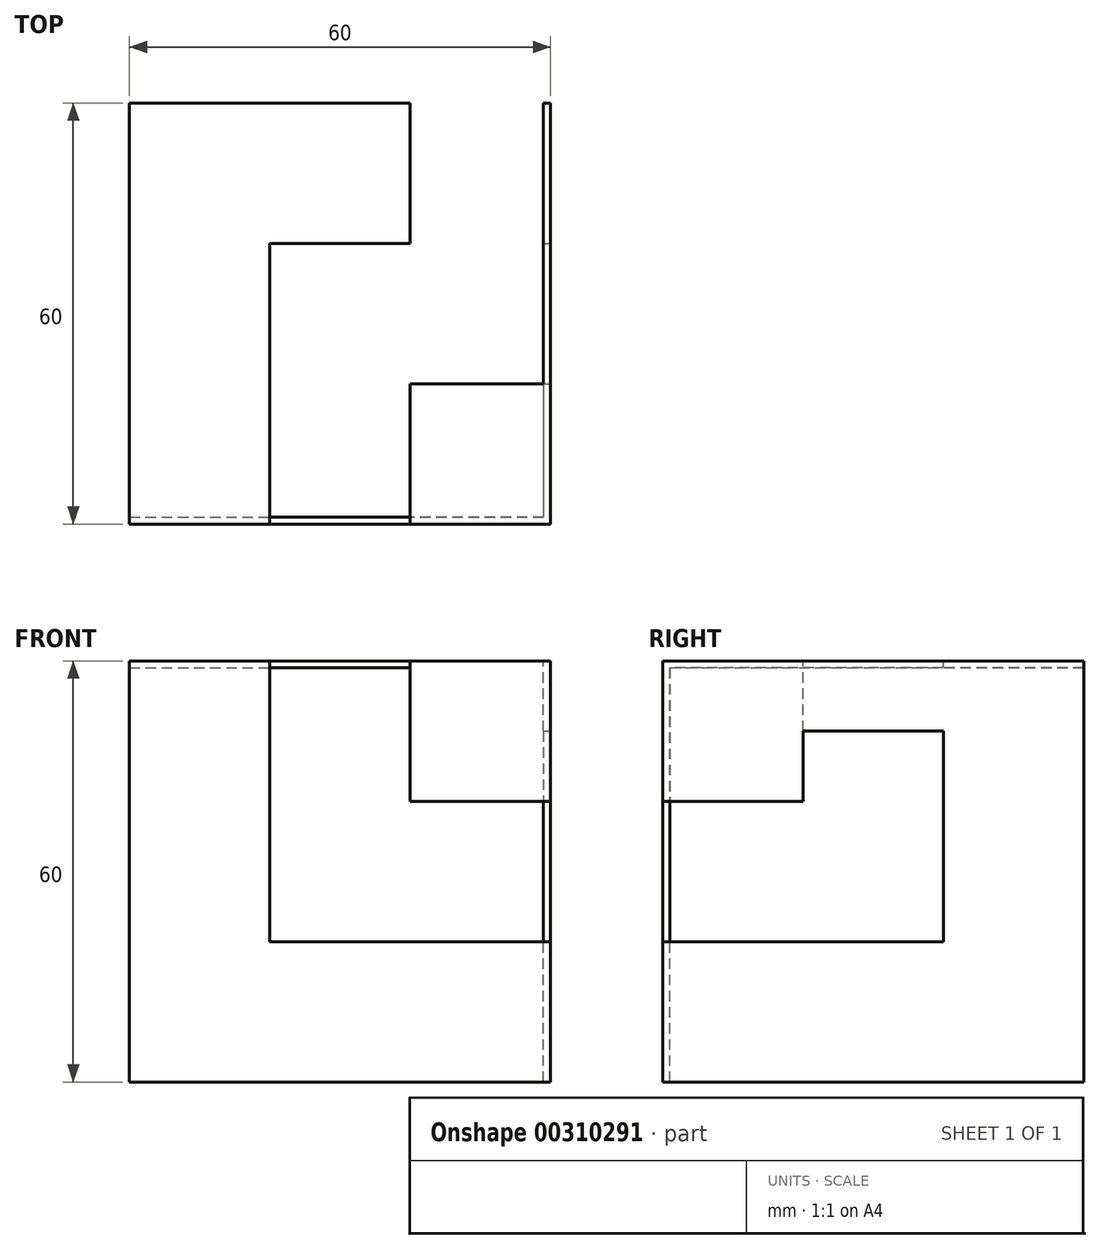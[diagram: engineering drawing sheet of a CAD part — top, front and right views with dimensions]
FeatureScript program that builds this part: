
annotation { "Feature Type Name" : "Feature", "Feature Type Description" : "" }
export const myFeature = defineFeature(function(context is Context, id is Id, definition is map)
    precondition{}
    {
        {
            var Q0;
            Q0=qCreatedBy(makeId("Top.planeOp"),FACE);
            var sketch = newSketch(context, id + "F0", { "sketchPlane" : qUnion([Q0])});
            skLineSegment(sketch, "E0.bottom", {"start": v(30, -30) * mm, "end": v(-30, -30) * mm});
            skLineSegment(sketch, "E0.top", {"start": v(30, 30) * mm, "end": v(-30, 30) * mm});
            skLineSegment(sketch, "E0.left", {"start": v(30, -30) * mm, "end": v(30, 30) * mm});
            skLineSegment(sketch, "E0.right", {"start": v(-30, -30) * mm, "end": v(-30, 30) * mm});
            skPoint(sketch, "E0.middle", {"position": v(0, 0) * mm});
            skSolve(sketch);
        }
        {
            var Q0;
            Q0=makeQuery(id+"F0.imprint","IMPRINT",FACE,{"disambiguationData":[TD([[makeQuery(id+"F0.imprint","IMPRINT",EDGE,{"derivedFrom":sQuery(id+"F0.wireOp",EDGE,"E0.bottom")}),-1.0]])]});
            extrude(context, id + "F1", {"entities" : qUnion([Q0]), "depth" : 60 * mm});
        }
        {
            var Q0;
            Q0=makeQuery(id+"F1.opExtrude","CAP_FACE",FACE,{"disambiguationData":[OSD([sQuery(id+"F0.wireOp",EDGE,"E0.bottom"),sQuery(id+"F0.wireOp",EDGE,"E0.top"),sQuery(id+"F0.wireOp",EDGE,"E0.left"),sQuery(id+"F0.wireOp",EDGE,"E0.right")])],"isStart":false});
            var sketch = newSketch(context, id + "F2", { "sketchPlane" : qUnion([Q0])});
            skLineSegment(sketch, "E1", {"start": v(30, -10) * mm, "end": v(10, -10) * mm});
            skLineSegment(sketch, "E2", {"start": v(10, -10) * mm, "end": v(10, -30) * mm});
            skLineSegment(sketch, "E3", {"start": v(-10, -30) * mm, "end": v(-10, 30) * mm});
            skLineSegment(sketch, "E4", {"start": v(-30, 10) * mm, "end": v(30, 10) * mm});
            skLineSegment(sketch, "E5", {"start": v(29, 10) * mm, "end": v(29, -10) * mm});
            skLineSegment(sketch, "E6", {"start": v(-10, -29) * mm, "end": v(10, -29) * mm});
            skLineSegment(sketch, "E7", {"start": v(10, 10) * mm, "end": v(10, 30) * mm});
            skLineSegment(sketch, "E8", {"start": v(29, 10) * mm, "end": v(29, 30) * mm});
            skSolve(sketch);
        }
        {
            var Q0;
            Q0 = qSketchRegion(id + "F2", true);
            var Q1;
            {var subQ2=sQuery(id+"F2.wireOp",EDGE,"E7");Q1=makeQuery(id+"F2.imprint","IMPRINT",FACE,{"disambiguationData":[TD([[makeQuery(id+"F2.imprint","IMPRINT",EDGE,{"derivedFrom":subQ2}),-1.0]])]});}
            extrude(context, id + "F3", {"entities" : qUnion([Q0, Q1]), "operationType" : NewBodyOperationType.REMOVE, "endBound" : BoundingType.THROUGH_ALL, "oppositeDirection" : true, "depth" : 25 * mm});
        }
        {
            var Q0;
            Q0=makeQuery(id+"F1.opExtrude","SWEPT_FACE",FACE,{"disambiguationData":[OSD([sQuery(id+"F0.wireOp",EDGE,"E0.bottom")])]});
            var sketch = newSketch(context, id + "F4", { "sketchPlane" : qUnion([Q0])});
            skLineSegment(sketch, "E9", {"start": v(-10, 60) * mm, "end": v(-10, 0) * mm});
            skLineSegment(sketch, "E10", {"start": v(10, 60) * mm, "end": v(10, 40) * mm});
            skLineSegment(sketch, "E11", {"start": v(10, 40) * mm, "end": v(30, 40) * mm});
            skLineSegment(sketch, "E12", {"start": v(30, 20) * mm, "end": v(-30, 20) * mm});
            skLineSegment(sketch, "E13", {"start": v(10, 59) * mm, "end": v(-10, 59) * mm});
            skLineSegment(sketch, "E14", {"start": v(29, 40) * mm, "end": v(29, 20) * mm});
            skSolve(sketch);
        }
        {
            var Q0;
            Q0 = qSketchRegion(id + "F4", true);
            extrude(context, id + "F5", {"entities" : qUnion([Q0]), "operationType" : NewBodyOperationType.REMOVE, "endBound" : BoundingType.THROUGH_ALL, "oppositeDirection" : true, "depth" : 25 * mm});
        }
        {
            var Q0;
            Q0=makeQuery(id+"F5.boolean.opBoolean","COPY",FACE,{"disambiguationData":[TD([makeQuery(id+"F1.opExtrude","SWEPT_FACE",FACE,{"disambiguationData":[OSD([sQuery(id+"F0.wireOp",EDGE,"E0.bottom")])]})])],"derivedFrom":makeQuery(id+"F5.opExtrude","SWEPT_FACE",FACE,{"disambiguationData":[OSD([sQuery(id+"F4.wireOp",EDGE,"E12")])]})});
            var sketch = newSketch(context, id + "F6", { "sketchPlane" : qUnion([Q0])});
            skLineSegment(sketch, "E15", {"start": v(10, -29) * mm, "end": v(29, -29) * mm});
            skPoint(sketch, "E15.endSnap0", {"position": v(29, -20) * mm});
            skSolve(sketch);
        }
        {
            var Q0;
            {var subQ0=sQuery(id+"F6.wireOp",EDGE,"E15");Q0=makeQuery(id+"F6.imprint","IMPRINT",FACE,{"disambiguationData":[TD([[makeQuery(id+"F6.imprint","IMPRINT",EDGE,{"derivedFrom":subQ0}),1.0]])]});}
            var Q1;
            Q1=makeQuery(id+"F5.boolean.opBoolean","COPY",FACE,{"disambiguationData":[TD([makeQuery(id+"F1.opExtrude","SWEPT_FACE",FACE,{"disambiguationData":[OSD([sQuery(id+"F0.wireOp",EDGE,"E0.top")])]})])],"derivedFrom":makeQuery(id+"F5.opExtrude","SWEPT_FACE",FACE,{"disambiguationData":[OSD([sQuery(id+"F4.wireOp",EDGE,"E12")])]})});
            extrude(context, id + "F7", {"entities" : qUnion([Q0, Q1]), "operationType" : NewBodyOperationType.REMOVE, "oppositeDirection" : true, "depth" : 25 * mm});
        }
        {
            var Q0;
            Q0=makeQuery(id+"F1.opExtrude","SWEPT_FACE",FACE,{"disambiguationData":[OSD([sQuery(id+"F0.wireOp",EDGE,"E0.left")])]});
            var sketch = newSketch(context, id + "F8", { "sketchPlane" : qUnion([Q0])});
            skLineSegment(sketch, "E16", {"start": v(-30, 20) * mm, "end": v(30, 20) * mm});
            skLineSegment(sketch, "E17", {"start": v(10, 0) * mm, "end": v(10, 60) * mm});
            skLineSegment(sketch, "E18", {"start": v(-10, 60) * mm, "end": v(-10, 40) * mm});
            skLineSegment(sketch, "E19", {"start": v(-10, 40) * mm, "end": v(-30, 40) * mm});
            skLineSegment(sketch, "E20", {"start": v(10, 50) * mm, "end": v(-10, 50) * mm});
            skLineSegment(sketch, "E21", {"start": v(-29, 40) * mm, "end": v(-29, 20) * mm});
            skSolve(sketch);
        }
        {
            var Q0;
            {var subQ4=sQuery(id+"F8.wireOp",EDGE,"E20");Q0=makeQuery(id+"F8.imprint","IMPRINT",FACE,{"disambiguationData":[TD([[makeQuery(id+"F8.imprint","IMPRINT",EDGE,{"derivedFrom":subQ4}),1.0]])]});}
            extrude(context, id + "F9", {"entities" : qUnion([Q0]), "operationType" : NewBodyOperationType.REMOVE, "endBound" : BoundingType.THROUGH_ALL, "oppositeDirection" : true, "depth" : 25 * mm});
        }
        {
            var Q0;
            {var subQ0=sQuery(id+"F4.wireOp",EDGE,"E9");Q0=makeQuery(id+"F7.boolean.opBoolean","MERGE",FACE,{"derivedFrom":[makeQuery(id+"F5.boolean.opBoolean","MERGE",FACE,{"derivedFrom":[makeQuery(id+"F3.boolean.opBoolean","COPY",FACE,{"derivedFrom":makeQuery(id+"F3.opExtrude","SWEPT_FACE",FACE,{"disambiguationData":[OSD([sQuery(id+"F2.wireOp",EDGE,"E3")])]})}),makeQuery(id+"F5.opExtrude","SWEPT_FACE",FACE,{"disambiguationData":[OSD([subQ0])]})]}),makeQuery(id+"F7.opExtrude","SWEPT_FACE",FACE,{"disambiguationData":[OSD([subQ0,sQuery(id+"F4.wireOp",EDGE,"E12")])]})]});}
            var sketch = newSketch(context, id + "F10", { "sketchPlane" : qUnion([Q0])});
            skLineSegment(sketch, "E22", {"start": v(30, 59) * mm, "end": v(-30, 59) * mm});
            skLineSegment(sketch, "E23", {"start": v(-29, 59) * mm, "end": v(-29, 40) * mm});
            skSolve(sketch);
        }
        {
            var Q0;
            {var subQ14=sQuery(id+"F10.wireOp",EDGE,"E23");Q0=makeQuery(id+"F10.imprint","IMPRINT",FACE,{"disambiguationData":[TD([[makeQuery(id+"F10.imprint","IMPRINT",EDGE,{"derivedFrom":subQ14}),1.0]])]});}
            extrude(context, id + "F11", {"entities" : qUnion([Q0]), "operationType" : NewBodyOperationType.REMOVE, "endBound" : BoundingType.THROUGH_ALL, "oppositeDirection" : true, "depth" : 25 * mm});
        }
        {
            var Q0;
            Q0=makeQuery(id+"F1.opExtrude","SWEPT_FACE",FACE,{"disambiguationData":[OSD([sQuery(id+"F0.wireOp",EDGE,"E0.bottom")])]});
            var sketch = newSketch(context, id + "F12", { "sketchPlane" : qUnion([Q0])});
            skLineSegment(sketch, "E24", {"start": v(-10, 60) * mm, "end": v(-10, 59) * mm});
            skLineSegment(sketch, "E25", {"start": v(10, 59) * mm, "end": v(10, 60) * mm});
            skLineSegment(sketch, "E26", {"start": v(29, 40) * mm, "end": v(30, 40) * mm});
            skLineSegment(sketch, "E27", {"start": v(29, 20) * mm, "end": v(30, 20) * mm});
            skSolve(sketch);
        }
        {
            var Q0;
            {var subQ0=sQuery(id+"F12.wireOp",EDGE,"E26");Q0=makeQuery(id+"F12.imprint","IMPRINT",FACE,{"disambiguationData":[TD([[makeQuery(id+"F12.imprint","IMPRINT",EDGE,{"derivedFrom":subQ0}),-1.0]])]});}
            var Q1;
            {var subQ0=sQuery(id+"F12.wireOp",EDGE,"E24");Q1=makeQuery(id+"F12.imprint","IMPRINT",FACE,{"disambiguationData":[TD([[makeQuery(id+"F12.imprint","IMPRINT",EDGE,{"derivedFrom":subQ0}),1.0]])]});}
            extrude(context, id + "F13", {"entities" : qUnion([Q0, Q1]), "operationType" : NewBodyOperationType.REMOVE, "oppositeDirection" : true, "depth" : 2 * mm});
        }
    });
